# Revit family: French-PGT-Aluminum_Preferred-FD750-Sidelited
name_source: partatom
category: Doors
revit_build: Autodesk Revit 2015 (Build: 20160512_1515(x64)
units: mm (PartAtom-declared; Revit-internal decimal feet)

## types (1)
- French Door Sidelite
    Analytic Construction = <None>
    Assembly Code = B2020110
    CL Offset From Exterior = 0' - 1 9/32"
    Color Glass = Glass - PGT - Clear
    Custom Design Note = Please reference the 'Product Style Guide' to see all standard configurations and restrictions before creating custom designs.  Please contact PGT Industries with any questions regarding custom designs.
    Description = Aluminum Preferred Sidelite
    Finish = Metal - PGT - Paint - White
    Full Frame = No
    Function = Exterior
    Grid = Yes
    Grid Layout Note = To edit the grid layout ensure the 'Grid' parameter is turned on and then select an option from the 'Grid Type' drop down.  Please refer to the 'Product Style Guide' for standard configurations and restrictions.
    Grid Type = Face_Based_Mullion_ Glass : 2C7R
    Height = 7' - 0"
    Manufacturer = PGT Industries
    Maximum Size = 36 11/16” x 95 3/4”
    Minimum Size = Contact Manufacturer
    Model = FD750
    Narrow Frame = Yes
    Product Page URL = http://www.pgtindustries.com
    Product Style Guide = http://www.pgtindustries.com
    Rough Height = 7' - 0"
    Rough Width = 2' - 0"
    Type Comments = Sidelite
    URL = http://www.pgtindustries.com
    Wall Closure = By host
    Width = 2' - 0"

## geometry (parser evidence)
native form markers: Sweep x21
no freeform markers — native parametric forms only
